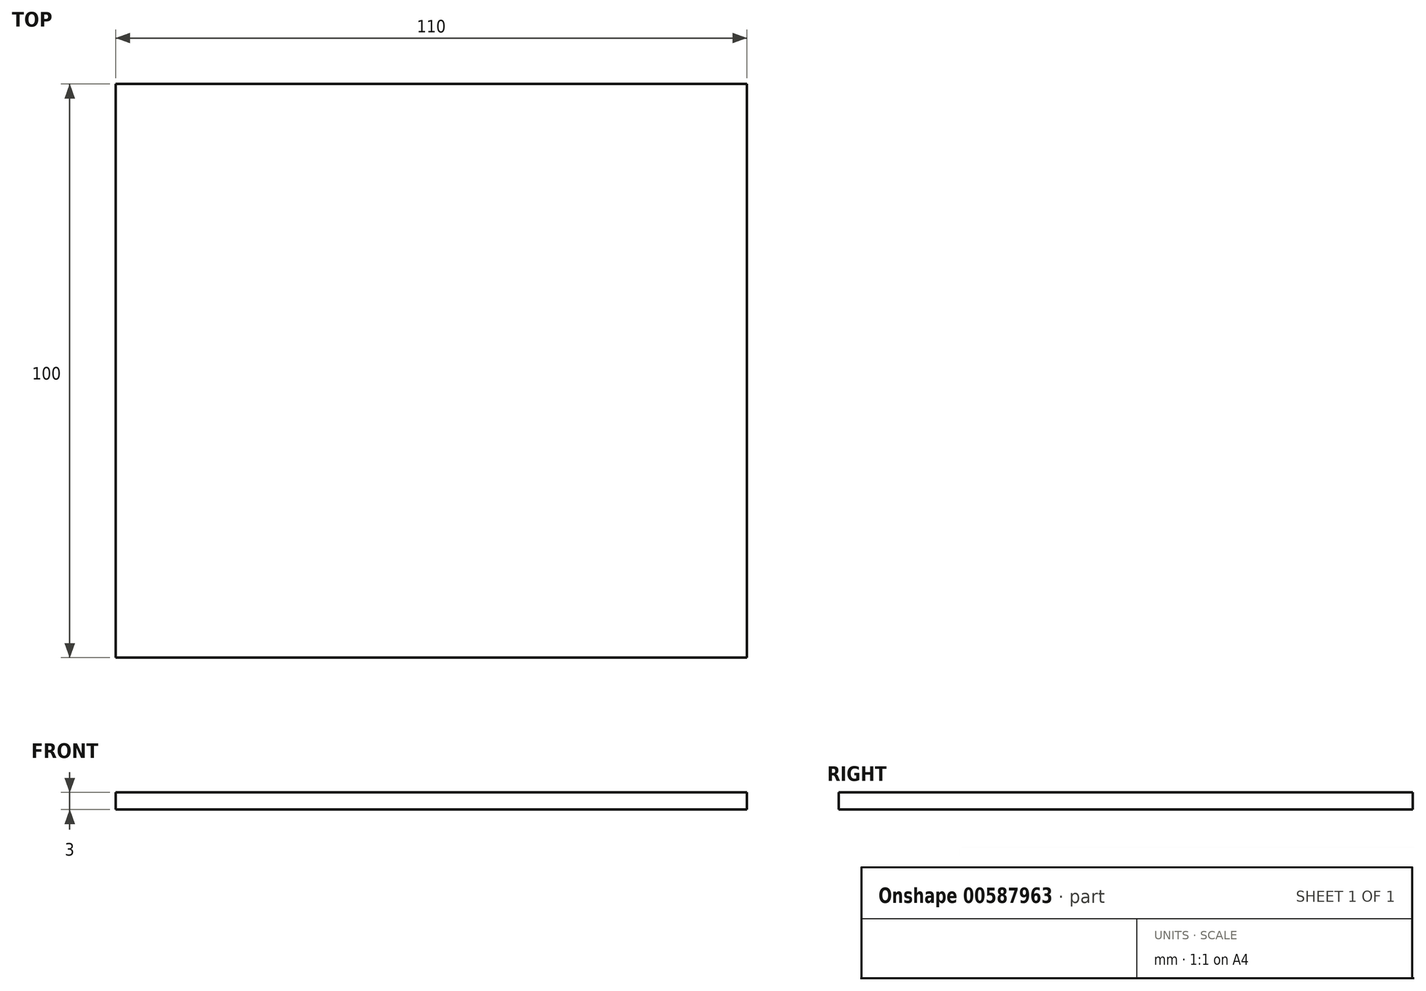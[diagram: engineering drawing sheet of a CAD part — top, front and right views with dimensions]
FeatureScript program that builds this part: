
annotation { "Feature Type Name" : "Feature", "Feature Type Description" : "" }
export const myFeature = defineFeature(function(context is Context, id is Id, definition is map)
    precondition{}
    {
        {
            var Q0;
            Q0=qCreatedBy(makeId("Top.planeOp"),FACE);
            var sketch = newSketch(context, id + "F0", { "sketchPlane" : qUnion([Q0])});
            skLineSegment(sketch, "E0.bottom", {"start": v(0, 0) * mm, "end": v(-110, 0) * mm});
            skLineSegment(sketch, "E0.top", {"start": v(0, 100) * mm, "end": v(-110, 100) * mm});
            skLineSegment(sketch, "E0.left", {"start": v(0, 0) * mm, "end": v(0, 100) * mm});
            skLineSegment(sketch, "E0.right", {"start": v(-110, 0) * mm, "end": v(-110, 100) * mm});
            skSolve(sketch);
        }
        {
            var Q0;
            Q0 = qSketchRegion(id + "F0", true);
            extrude(context, id + "F1", {"entities" : qUnion([Q0]), "depth" : (3) * mm, "offsetDistance" : 25 * mm});
        }
    });
